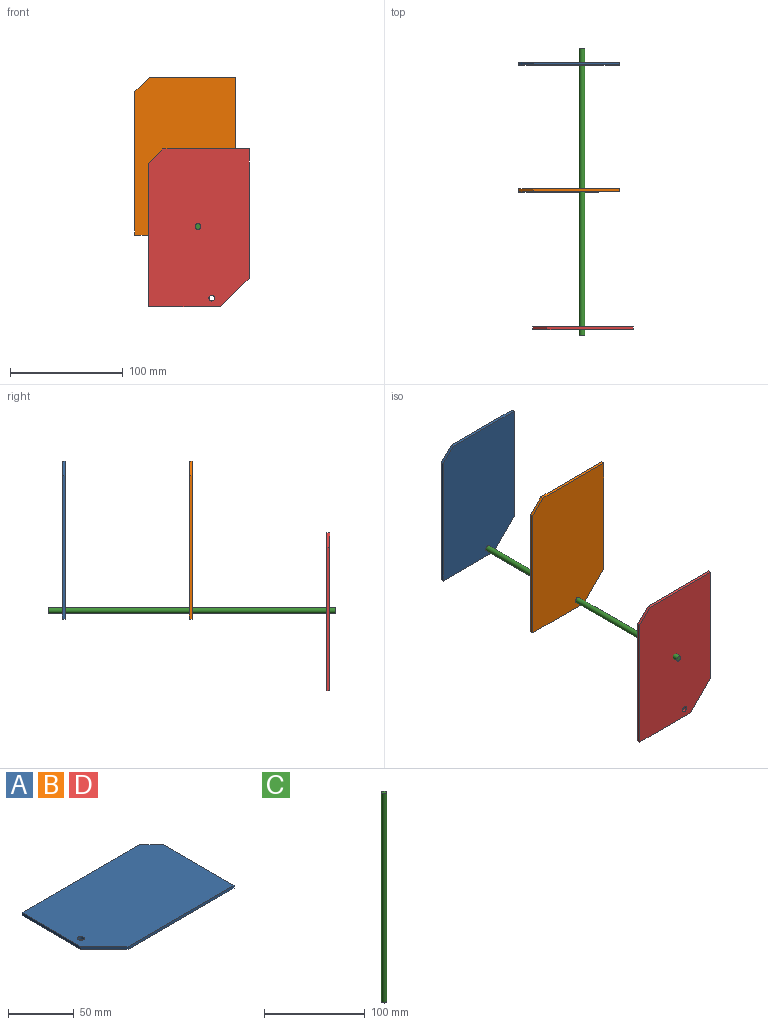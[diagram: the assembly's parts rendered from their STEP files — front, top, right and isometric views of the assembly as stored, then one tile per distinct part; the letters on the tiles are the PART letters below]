
ASSEMBLY  parts=4 mates=3
PART A: 9 faces, bbox 139.7x88.9x2.5 mm
  f0: plane 114.3x2.54mm, normal (0,-1,0), area 290.3mm2, adj f1,f5,f7,f8
  f1: plane 76.2x2.54mm, normal (1,0,0), area 193.5mm2, adj f0,f2,f7,f8
  f2: plane 12.7x12.7mm, normal (0.71,0.71,0), area 45.6mm2, adj f1,f3,f7,f8
  f3: plane 127x2.54mm, normal (0,1,0), area 322.6mm2, adj f2,f4,f7,f8
  f4: plane 63.5x2.54mm, normal (-1,0,0), area 161.3mm2, adj f3,f5,f7,f8
  f5: plane 25.4x25.4mm, normal (-0.71,-0.71,0), area 91.2mm2, adj f0,f4,f7,f8
  f6: cylinder r=2.54mm len=5.08mm, axis (0,0,-1), area 40.5mm2, adj f7,f8
  f7: plane 139.7x88.9mm, normal (0,0,1), area 11995.8mm2, adj f0,f1,f2,f3,f4,f5,f6
  f8: plane 139.7x88.9mm, normal (0,0,-1), area 11995.8mm2, adj f0,f1,f2,f3,f4,f5,f6
PART B: same geometry as A
PART C: 3 faces, bbox 5.1x5.1x254 mm
  f0: cylinder r=2.54mm len=254mm, axis (0,0,-1), area 4053.7mm2, adj f1,f2
  f1: plane 5.08x5.08mm, normal (0,0,1), area 20.3mm2, adj f0
  f2: plane 5.08x5.08mm, normal (0,0,-1), area 20.3mm2, adj f0
PART D: same geometry as A
PLACE A rot(axis=(0.58,-0.58,0.58),120deg) t=(-12.57,-203.94,-227.68)mm
PLACE B rot(axis=(0.58,-0.58,0.58),120deg) t=(-12.57,-316.21,-227.68)mm
PLACE C rot(axis=(-1,0,0),90deg) t=(-45.59,-445.75,-359.76)mm
PLACE D rot(axis=(0.58,-0.58,0.58),120deg) t=(-0.43,-438.13,-291.23)mm
MATE revolute C.f0 <-> D.f6  axis (0,-1,0) through (-45.59,-318.75,-359.76)mm
MATE revolute C.f0 <-> B.f6  axis (0,-1,0) through (-45.59,-318.75,-359.76)mm
MATE planar D.f7 <-> C.f0  axis (0,-1,0) through (-45.59,-440.67,-359.76)mm
